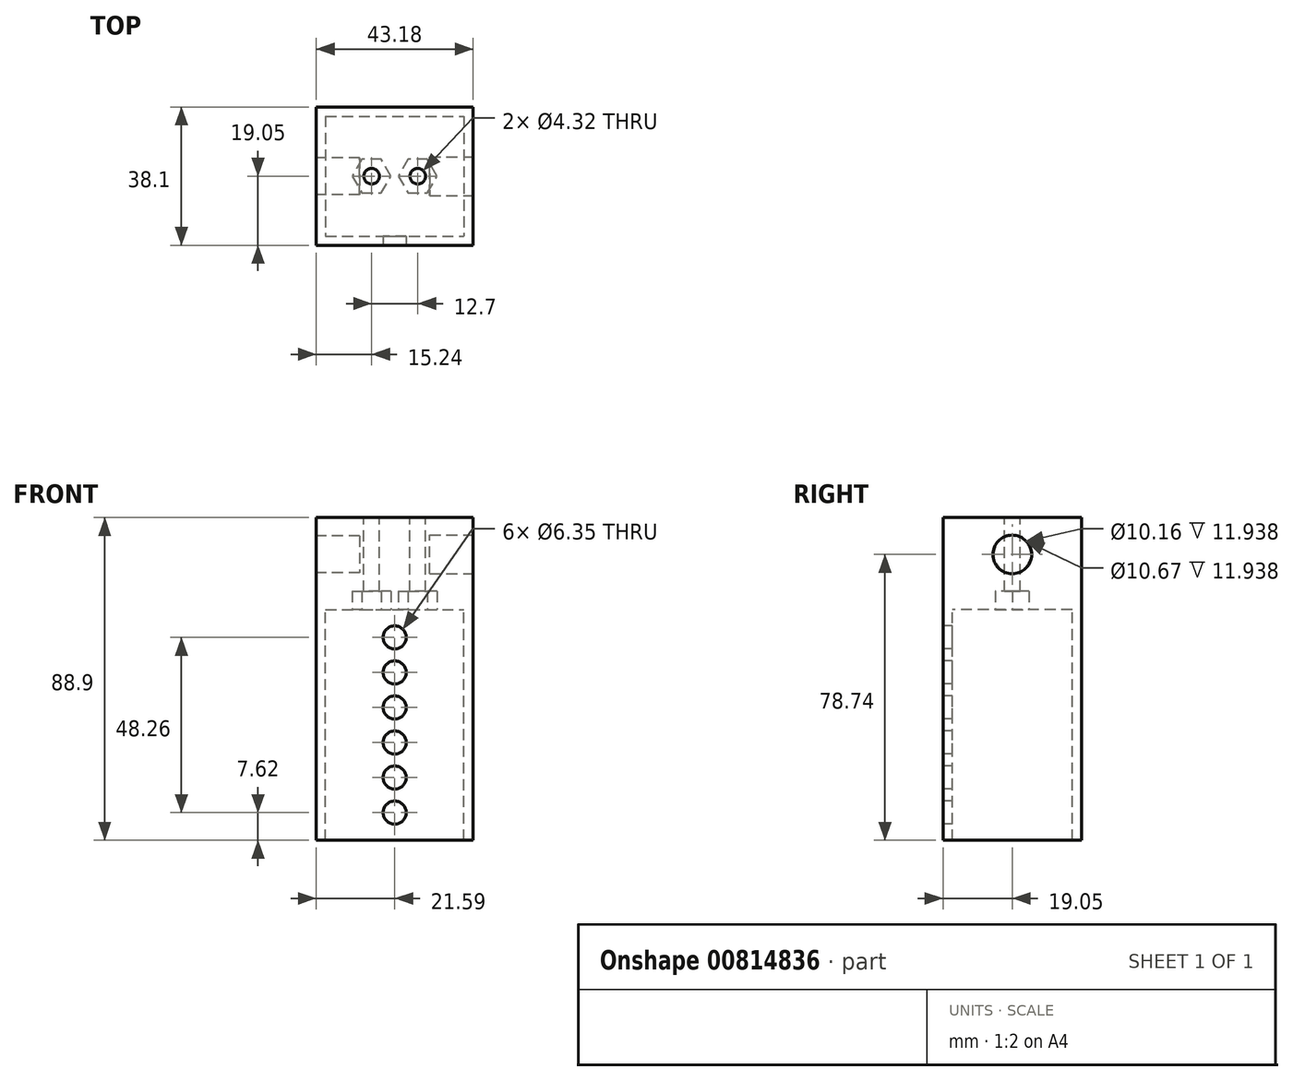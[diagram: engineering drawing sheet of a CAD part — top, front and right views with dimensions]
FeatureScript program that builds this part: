
annotation { "Feature Type Name" : "Feature", "Feature Type Description" : "" }
export const myFeature = defineFeature(function(context is Context, id is Id, definition is map)
    precondition{}
    {
        {
            var Q0;
            Q0=qCreatedBy(makeId("Top.planeOp"),FACE);
            var sketch = newSketch(context, id + "F0", { "sketchPlane" : qUnion([Q0])});
            skLineSegment(sketch, "E0.bottom", {"start": v(-21.59, 19.05) * mm, "end": v(21.6, 19.05) * mm});
            skLineSegment(sketch, "E0.top", {"start": v(-21.6, -19.05) * mm, "end": v(21.59, -19.05) * mm});
            skLineSegment(sketch, "E0.left", {"start": v(-21.59, 19.05) * mm, "end": v(-21.6, -19.05) * mm});
            skLineSegment(sketch, "E0.right", {"start": v(21.6, 19.05) * mm, "end": v(21.59, -19.05) * mm});
            skPoint(sketch, "E0.middle", {"position": v(0, 0) * mm});
            skCircle(sketch, "E1", {"center": v(-6.35, 0) * mm, "radius": 2.16 * mm});
            skCircle(sketch, "E2", {"center": v(6.35, 0) * mm, "radius": 2.16 * mm});
            skLineSegment(sketch, "E3.bottom", {"start": v(-19.05, 16.51) * mm, "end": v(19.05, 16.51) * mm});
            skLineSegment(sketch, "E3.top", {"start": v(-19.05, -16.51) * mm, "end": v(19.05, -16.51) * mm});
            skLineSegment(sketch, "E3.left", {"start": v(-19.05, 16.51) * mm, "end": v(-19.05, -16.51) * mm});
            skLineSegment(sketch, "E3.right", {"start": v(19.05, 16.51) * mm, "end": v(19.05, -16.51) * mm});
            skSolve(sketch);
        }
        {
            var Q0;
            Q0 = qSketchRegion(id + "F0", true);
            extrude(context, id + "F1", {"entities" : qUnion([Q0]), "endBound" : BoundingType.SYMMETRIC, "oppositeDirection" : true, "depth" : 88.9 * mm, "offsetDistance" : 25.4 * mm});
        }
        {
            var Q0;
            Q0=makeQuery(id+"F1.opExtrude","CAP_FACE",FACE,{"disambiguationData":[OSD([sQuery(id+"F0.wireOp",EDGE,"E0.bottom"),sQuery(id+"F0.wireOp",EDGE,"E0.top"),sQuery(id+"F0.wireOp",EDGE,"E0.left"),sQuery(id+"F0.wireOp",EDGE,"E0.right"),sQuery(id+"F0.wireOp",EDGE,"E3.bottom"),sQuery(id+"F0.wireOp",EDGE,"E3.top"),sQuery(id+"F0.wireOp",EDGE,"E3.left"),sQuery(id+"F0.wireOp",EDGE,"E3.right")])],"isStart":true});
            var sketch = newSketch(context, id + "F2", { "sketchPlane" : qUnion([Q0])});
            skPoint(sketch, "E4.middle", {"position": v(0, 0) * mm});
            skCircle(sketch, "E5", {"center": v(-6.35, 0) * mm, "radius": 2.16 * mm});
            skCircle(sketch, "E6", {"center": v(6.35, 0) * mm, "radius": 2.16 * mm});
            skLineSegment(sketch, "E7.bottom", {"start": v(-19.05, 16.51) * mm, "end": v(19.05, 16.51) * mm});
            skLineSegment(sketch, "E7.top", {"start": v(-19.05, -16.51) * mm, "end": v(19.05, -16.51) * mm});
            skLineSegment(sketch, "E7.left", {"start": v(-19.05, 16.51) * mm, "end": v(-19.05, -16.51) * mm});
            skLineSegment(sketch, "E7.right", {"start": v(19.05, 16.51) * mm, "end": v(19.05, -16.51) * mm});
            skSolve(sketch);
        }
        {
            var Q0;
            Q0 = qSketchRegion(id + "F2", true);
            var Q1;
            Q1=makeQuery(id+"F2.imprint","IMPRINT",FACE,{"disambiguationData":[TD([[makeQuery(id+"F2.imprint","IMPRINT",EDGE,{"derivedFrom":sQuery(id+"F2.wireOp",EDGE,"E5")}),-1.0]])]});
            extrude(context, id + "F3", {"entities" : qUnion([Q0, Q1]), "operationType" : NewBodyOperationType.ADD, "oppositeDirection" : true, "depth" : 25.4 * mm, "offsetDistance" : 25.4 * mm});
        }
        {
            var Q0;
            Q0=makeQuery(id+"F3.opExtrude","CAP_FACE",FACE,{"disambiguationData":[OSD([sQuery(id+"F2.wireOp",EDGE,"E4.bottom"),sQuery(id+"F2.wireOp",EDGE,"E4.top"),sQuery(id+"F2.wireOp",EDGE,"E4.left"),sQuery(id+"F2.wireOp",EDGE,"E4.right"),sQuery(id+"F2.wireOp",EDGE,"E5"),sQuery(id+"F2.wireOp",EDGE,"E6")])],"isStart":false});
            var sketch = newSketch(context, id + "F4", { "sketchPlane" : qUnion([Q0])});
            skCircle(sketch, "E8.0", {"center": v(-6.35, 0) * mm, "radius": 2.16 * mm});
            skCircle(sketch, "E9.0", {"center": v(6.35, 0) * mm, "radius": 2.16 * mm});
            skCircle(sketch, "E10", {"center": v(-6.35, 0) * mm, "radius": 5.33 * mm, "construction": true});
            skLineSegment(sketch, "E11.0", {"start": v(-9.02, 4.62) * mm, "end": v(-3.68, 4.62) * mm});
            skLineSegment(sketch, "E11.1", {"start": v(-3.68, 4.62) * mm, "end": v(-1.02, 0) * mm});
            skLineSegment(sketch, "E11.2", {"start": v(-1.02, 0) * mm, "end": v(-3.68, -4.62) * mm});
            skLineSegment(sketch, "E11.3", {"start": v(-3.68, -4.62) * mm, "end": v(-9.02, -4.62) * mm});
            skLineSegment(sketch, "E11.4", {"start": v(-9.02, -4.62) * mm, "end": v(-11.68, 0) * mm});
            skLineSegment(sketch, "E11.5", {"start": v(-11.68, 0) * mm, "end": v(-9.02, 4.62) * mm});
            skCircle(sketch, "E12", {"center": v(6.35, 0) * mm, "radius": 5.33 * mm, "construction": true});
            skLineSegment(sketch, "E13.0", {"start": v(3.68, 4.62) * mm, "end": v(9.02, 4.62) * mm});
            skLineSegment(sketch, "E13.1", {"start": v(9.02, 4.62) * mm, "end": v(11.68, 0) * mm});
            skLineSegment(sketch, "E13.2", {"start": v(11.68, 0) * mm, "end": v(9.02, -4.62) * mm});
            skLineSegment(sketch, "E13.3", {"start": v(9.02, -4.62) * mm, "end": v(3.68, -4.62) * mm});
            skLineSegment(sketch, "E13.4", {"start": v(3.68, -4.62) * mm, "end": v(1.02, 0) * mm});
            skLineSegment(sketch, "E13.5", {"start": v(1.02, 0) * mm, "end": v(3.68, 4.62) * mm});
            skSolve(sketch);
        }
        {
            var Q0;
            Q0=makeQuery(id+"F4.imprint","IMPRINT",FACE,{"disambiguationData":[TD([[makeQuery(id+"F4.imprint","IMPRINT",EDGE,{"derivedFrom":sQuery(id+"F4.wireOp",EDGE,"E9.0")}),1.0]])]});
            var Q1;
            Q1=makeQuery(id+"F4.imprint","IMPRINT",FACE,{"disambiguationData":[TD([[makeQuery(id+"F4.imprint","IMPRINT",EDGE,{"derivedFrom":sQuery(id+"F4.wireOp",EDGE,"E8.0")}),1.0]])]});
            extrude(context, id + "F5", {"entities" : qUnion([Q0, Q1]), "operationType" : NewBodyOperationType.REMOVE, "oppositeDirection" : true, "depth" : 5.08 * mm, "offsetDistance" : 25.4 * mm});
        }
        {
            var Q0;
            Q0=makeQuery(id+"F1.opExtrude","SWEPT_FACE",FACE,{"disambiguationData":[OSD([sQuery(id+"F0.wireOp",EDGE,"E0.top")])]});
            var sketch = newSketch(context, id + "F6", { "sketchPlane" : qUnion([Q0])});
            skLineSegment(sketch, "E14", {"start": v(0, 44.45) * mm, "end": v(0, 19.05) * mm, "construction": true});
            skCircle(sketch, "E15", {"center": v(0, 11.43) * mm, "radius": 3.18 * mm});
            skCircle(sketch, "E16", {"center": v(0, 1.78) * mm, "radius": 3.18 * mm});
            skCircle(sketch, "E17", {"center": v(0, -7.87) * mm, "radius": 3.18 * mm});
            skCircle(sketch, "E18", {"center": v(0, -17.53) * mm, "radius": 3.17 * mm});
            skCircle(sketch, "E19", {"center": v(0, -27.18) * mm, "radius": 3.18 * mm});
            skCircle(sketch, "E20", {"center": v(0, -36.83) * mm, "radius": 3.18 * mm});
            skSolve(sketch);
        }
        {
            var Q0;
            Q0 = qSketchRegion(id + "F6", true);
            extrude(context, id + "F7", {"entities" : qUnion([Q0]), "operationType" : NewBodyOperationType.REMOVE, "oppositeDirection" : true, "depth" : 16.26 * mm, "offsetDistance" : 25.4 * mm});
        }
        {
            var Q0;
            Q0=makeQuery(id+"F1.opExtrude","SWEPT_FACE",FACE,{"disambiguationData":[OSD([sQuery(id+"F0.wireOp",EDGE,"E0.left")])]});
            var sketch = newSketch(context, id + "F8", { "sketchPlane" : qUnion([Q0])});
            skCircle(sketch, "E21", {"center": v(0, 34.3) * mm, "radius": 5.08 * mm});
            skPoint(sketch, "E21.centerSnap0", {"position": v(0, 44.45) * mm});
            skSolve(sketch);
        }
        {
            var Q0;
            Q0=makeQuery(id+"F8.imprint","IMPRINT",FACE,{"disambiguationData":[TD([[makeQuery(id+"F8.imprint","IMPRINT",EDGE,{"derivedFrom":sQuery(id+"F8.wireOp",EDGE,"E21")}),1.0]])]});
            extrude(context, id + "F9", {"entities" : qUnion([Q0]), "operationType" : NewBodyOperationType.REMOVE, "oppositeDirection" : true, "depth" : 11.94 * mm, "offsetDistance" : 25.4 * mm});
        }
        {
            var Q0;
            Q0=makeQuery(id+"F1.opExtrude","SWEPT_FACE",FACE,{"disambiguationData":[OSD([sQuery(id+"F0.wireOp",EDGE,"E0.right")])]});
            var sketch = newSketch(context, id + "F10", { "sketchPlane" : qUnion([Q0])});
            skCircle(sketch, "E22", {"center": v(0, 34.3) * mm, "radius": 5.33 * mm});
            skPoint(sketch, "E22.centerSnap0", {"position": v(0, 44.45) * mm});
            skSolve(sketch);
        }
        {
            var Q0;
            Q0=makeQuery(id+"F10.imprint","IMPRINT",FACE,{"disambiguationData":[TD([[makeQuery(id+"F10.imprint","IMPRINT",EDGE,{"derivedFrom":sQuery(id+"F10.wireOp",EDGE,"E22")}),1.0]])]});
            extrude(context, id + "F11", {"entities" : qUnion([Q0]), "operationType" : NewBodyOperationType.REMOVE, "oppositeDirection" : true, "depth" : 11.94 * mm, "offsetDistance" : 25.4 * mm});
        }
    });
